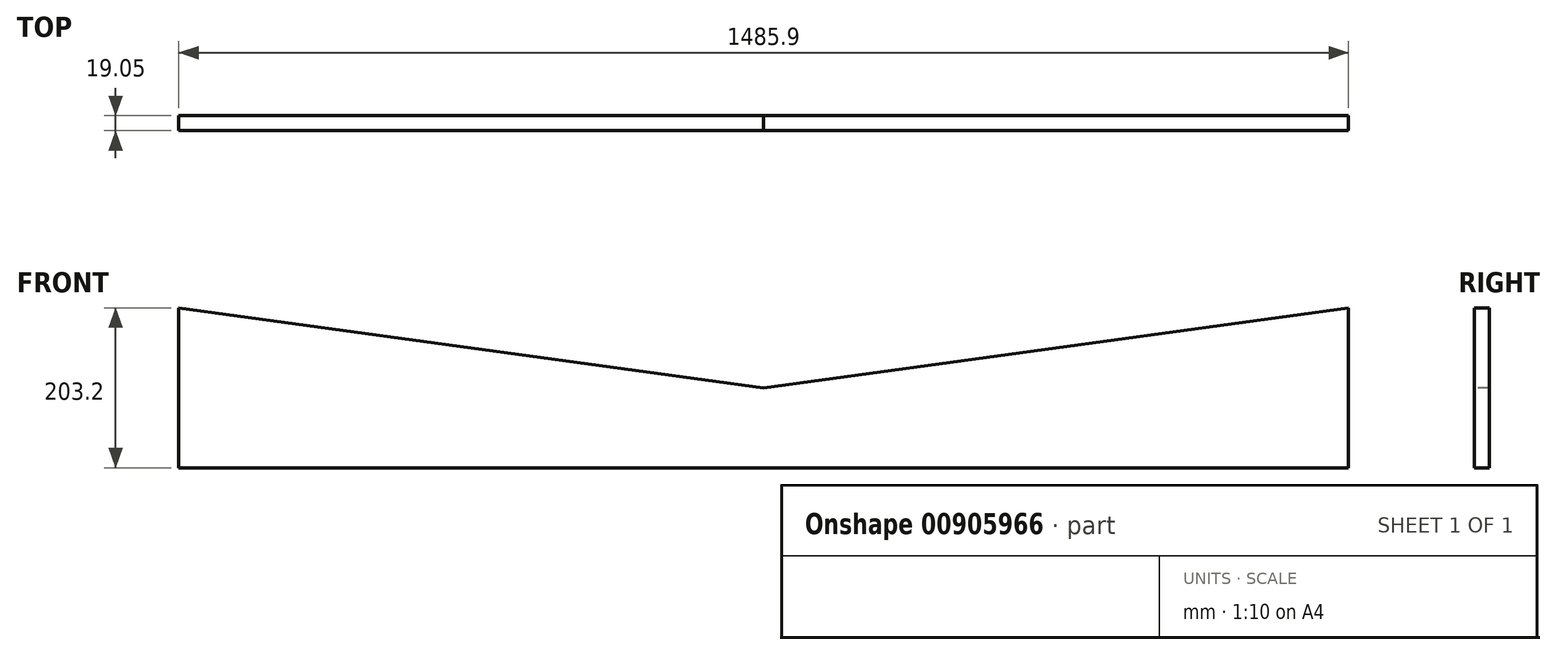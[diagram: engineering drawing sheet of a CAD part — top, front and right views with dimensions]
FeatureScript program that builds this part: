
annotation { "Feature Type Name" : "Feature", "Feature Type Description" : "" }
export const myFeature = defineFeature(function(context is Context, id is Id, definition is map)
    precondition{}
    {
        {
            var Q0;
            Q0=qCreatedBy(makeId("Front.planeOp"),FACE);
            var sketch = newSketch(context, id + "F0", { "sketchPlane" : qUnion([Q0])});
            skLineSegment(sketch, "E0.bottom", {"start": v(0, 0) * mm, "end": v(1485.9, 0) * mm});
            skLineSegment(sketch, "E0.top", {"start": v(0, 203.2) * mm, "end": v(1485.9, 203.2) * mm});
            skLineSegment(sketch, "E0.left", {"start": v(0, 0) * mm, "end": v(0, 203.2) * mm});
            skLineSegment(sketch, "E0.right", {"start": v(1485.9, 0) * mm, "end": v(1485.9, 203.2) * mm});
            skSolve(sketch);
        }
        {
            var Q0;
            Q0 = qSketchRegion(id + "F0", true);
            extrude(context, id + "F1", {"entities" : qUnion([Q0]), "depth" : 19.05 * mm, "offsetDistance" : 25.4 * mm});
        }
        {
            var Q0;
            Q0=makeQuery(id+"F1.opExtrude","CAP_FACE",FACE,{"disambiguationData":[OSD([sQuery(id+"F0.wireOp",EDGE,"E0.bottom"),sQuery(id+"F0.wireOp",EDGE,"E0.top"),sQuery(id+"F0.wireOp",EDGE,"E0.left"),sQuery(id+"F0.wireOp",EDGE,"E0.right")])],"isStart":false});
            var sketch = newSketch(context, id + "F2", { "sketchPlane" : qUnion([Q0])});
            skLineSegment(sketch, "E1", {"start": v(0, 0) * mm, "end": v(742.95, 101.6) * mm, "construction": true});
            skLineSegment(sketch, "E2", {"start": v(742.95, 101.6) * mm, "end": v(1485.9, 0) * mm, "construction": true});
            skLineSegment(sketch, "E3", {"start": v(1485.9, 0) * mm, "end": v(0, 0) * mm, "construction": true});
            skLineSegment(sketch, "E4", {"start": v(742.95, 0) * mm, "end": v(742.95, 101.6) * mm, "construction": true});
            skLineSegment(sketch, "E5", {"start": v(0, 203.2) * mm, "end": v(742.95, 101.6) * mm});
            skLineSegment(sketch, "E6", {"start": v(1485.9, 203.2) * mm, "end": v(742.95, 101.6) * mm});
            skLineSegment(sketch, "E7", {"start": v(1485.9, 203.2) * mm, "end": v(0, 203.2) * mm});
            skSolve(sketch);
        }
        {
            var Q0;
            Q0=makeQuery(id+"F2.imprint","IMPRINT",FACE,{"disambiguationData":[TD([[makeQuery(id+"F2.imprint","IMPRINT",EDGE,{"derivedFrom":sQuery(id+"F2.wireOp",EDGE,"E5")}),1.0]])]});
            extrude(context, id + "F3", {"entities" : qUnion([Q0]), "operationType" : NewBodyOperationType.REMOVE, "endBound" : BoundingType.THROUGH_ALL, "oppositeDirection" : true, "depth" : 25.4 * mm, "offsetDistance" : 25.4 * mm});
        }
    });
